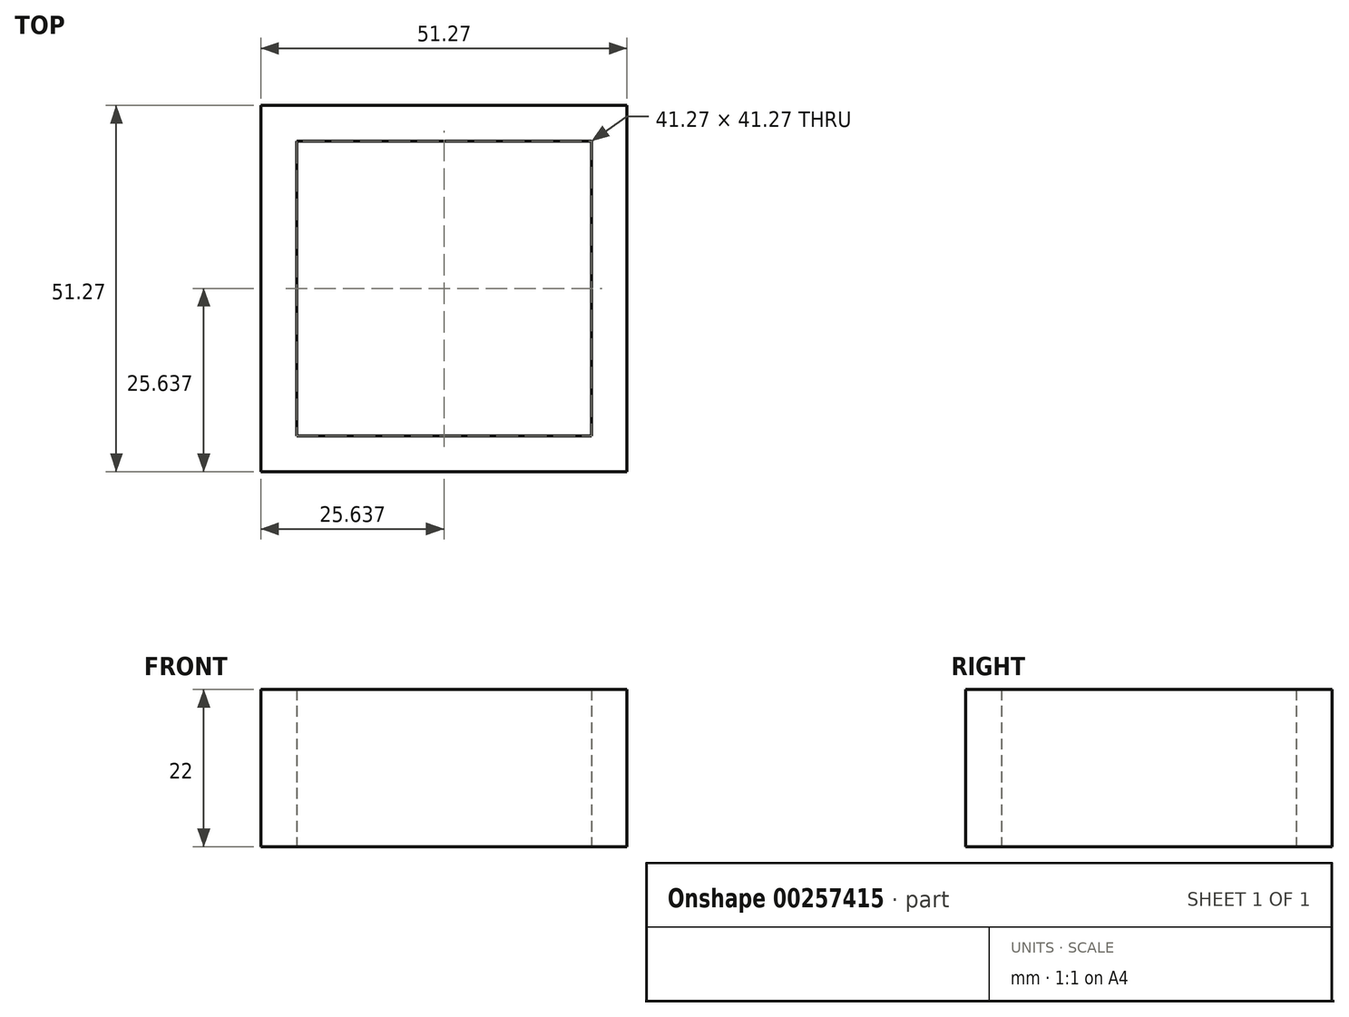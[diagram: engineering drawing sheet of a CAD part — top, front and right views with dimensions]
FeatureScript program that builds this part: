
annotation { "Feature Type Name" : "Feature", "Feature Type Description" : "" }
export const myFeature = defineFeature(function(context is Context, id is Id, definition is map)
    precondition{}
    {
        {
            var Q0;
            Q0=qCreatedBy(makeId("Top.planeOp"),FACE);
            var sketch = newSketch(context, id + "F0", { "sketchPlane" : qUnion([Q0])});
            skLineSegment(sketch, "E0.bottom", {"start": v(0, 0) * mm, "end": v(51.27, 0) * mm});
            skLineSegment(sketch, "E0.top", {"start": v(0, 51.28) * mm, "end": v(51.27, 51.28) * mm});
            skLineSegment(sketch, "E0.left", {"start": v(0, 0) * mm, "end": v(0, 51.28) * mm});
            skLineSegment(sketch, "E0.right", {"start": v(51.27, 0) * mm, "end": v(51.27, 51.27) * mm});
            skLineSegment(sketch, "E1.bottom", {"start": v(5, 5) * mm, "end": v(46.27, 5) * mm});
            skLineSegment(sketch, "E1.top", {"start": v(5, 46.28) * mm, "end": v(46.27, 46.28) * mm});
            skLineSegment(sketch, "E1.left", {"start": v(5, 5) * mm, "end": v(5, 46.28) * mm});
            skLineSegment(sketch, "E1.right", {"start": v(46.27, 5) * mm, "end": v(46.27, 46.28) * mm});
            skPoint(sketch, "E2.visualSharp", {"position": v(0, 0) * mm});
            skLineSegment(sketch, "E2.filletArc", {"start": v(0, 0) * mm, "end": v(0, 0) * mm});
            skPoint(sketch, "E3.visualSharp", {"position": v(51.27, 0) * mm});
            skLineSegment(sketch, "E3.filletArc", {"start": v(51.27, 0) * mm, "end": v(51.27, 0) * mm});
            skSolve(sketch);
        }
        {
            var Q0;
            Q0 = qSketchRegion(id + "F0", true);
            extrude(context, id + "F1", {"entities" : qUnion([Q0]), "depth" : 22 * mm});
        }
    });
